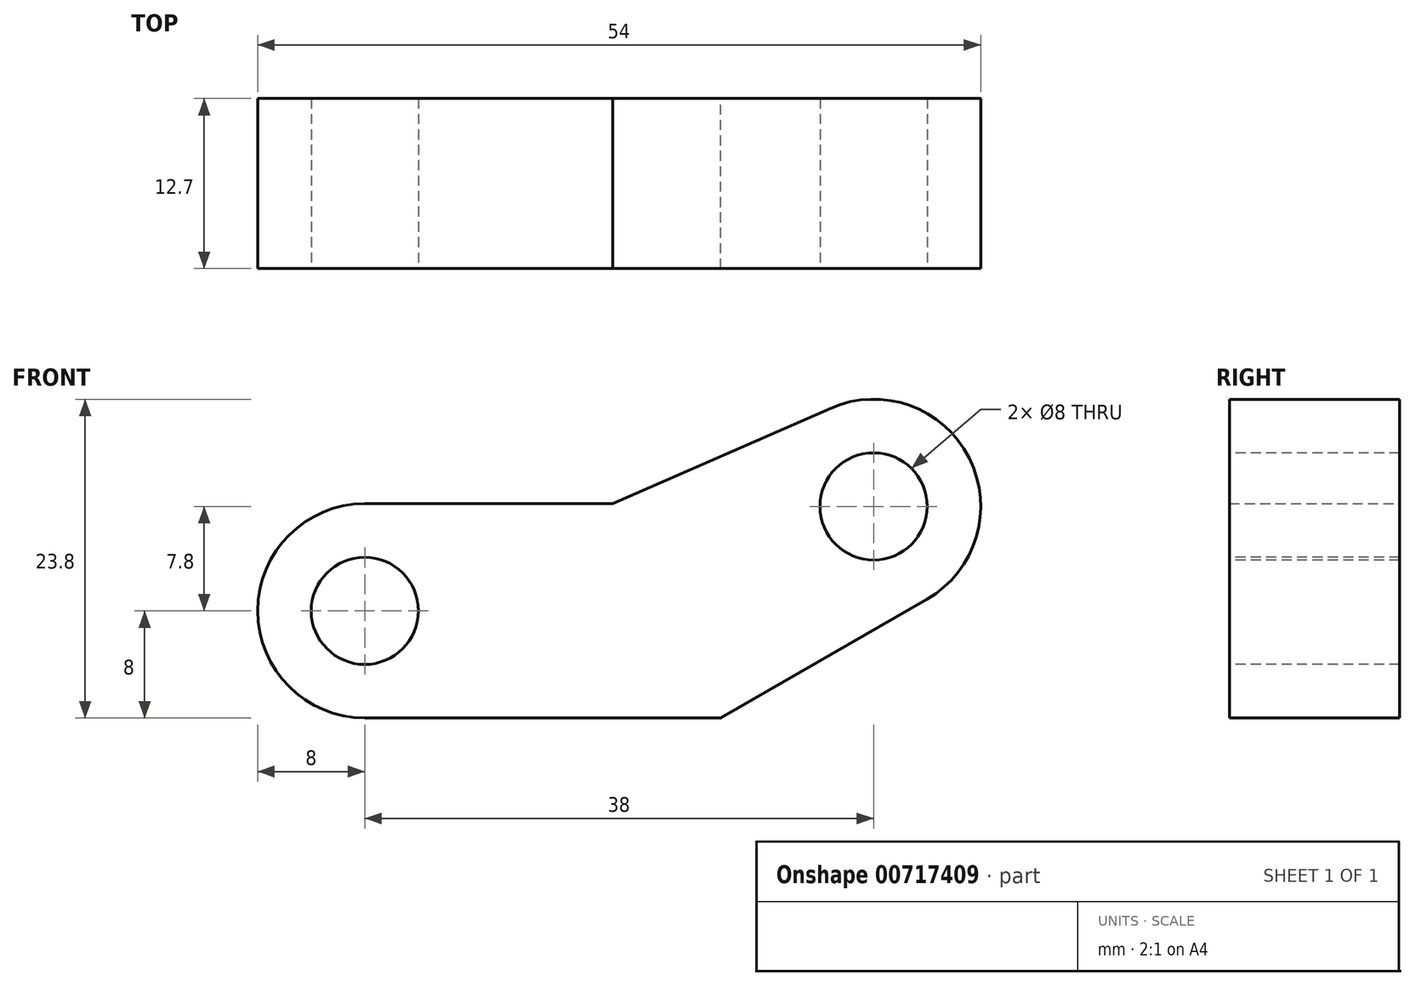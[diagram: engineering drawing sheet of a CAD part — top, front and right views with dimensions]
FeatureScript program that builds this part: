
annotation { "Feature Type Name" : "Feature", "Feature Type Description" : "" }
export const myFeature = defineFeature(function(context is Context, id is Id, definition is map)
    precondition{}
    {
        {
            var Q0;
            Q0=qCreatedBy(makeId("Front.planeOp"),FACE);
            var sketch = newSketch(context, id + "F0", { "sketchPlane" : qUnion([Q0])});
            skLineSegment(sketch, "E0", {"start": v(0, 0) * mm, "end": v(0, 7.8) * mm});
            skLineSegment(sketch, "E1", {"start": v(0, 0) * mm, "end": v(-38, 0) * mm});
            skCircle(sketch, "E2", {"center": v(-38, 0) * mm, "radius": 8 * mm});
            skCircle(sketch, "E3", {"center": v(0, 7.8) * mm, "radius": 8 * mm});
            skLineSegment(sketch, "E4", {"start": v(-38, -8) * mm, "end": v(-11.42, -8) * mm});
            skLineSegment(sketch, "E5", {"start": v(-11.42, -8) * mm, "end": v(3.99, 0.86) * mm});
            skLineSegment(sketch, "E6", {"start": v(-38, 8) * mm, "end": v(-19.5, 8) * mm});
            skLineSegment(sketch, "E7", {"start": v(-19.5, 8) * mm, "end": v(-3.2, 15.13) * mm});
            skSolve(sketch);
        }
        {
            var Q0;
            Q0 = qSketchRegion(id + "F0", true);
            extrude(context, id + "F1", {"entities" : qUnion([Q0]), "depth" : 12.7 * mm, "offsetDistance" : 25.4 * mm});
        }
        {
            var Q0;
            Q0=makeQuery(id+"F1.opExtrude","CAP_FACE",FACE,{"disambiguationData":[OSD([sQuery(id+"F0.wireOp",EDGE,"E2"),sQuery(id+"F0.wireOp",EDGE,"E3"),sQuery(id+"F0.wireOp",EDGE,"E4"),sQuery(id+"F0.wireOp",EDGE,"E5"),sQuery(id+"F0.wireOp",EDGE,"E6"),sQuery(id+"F0.wireOp",EDGE,"E7")])],"isStart":false});
            var sketch = newSketch(context, id + "F2", { "sketchPlane" : qUnion([Q0])});
            skCircle(sketch, "E8", {"center": v(-38, 0) * mm, "radius": 4 * mm});
            skCircle(sketch, "E9", {"center": v(0, 7.8) * mm, "radius": 4 * mm});
            skSolve(sketch);
        }
        {
            var Q0;
            Q0=makeQuery(id+"F2.imprint","IMPRINT",FACE,{"disambiguationData":[TD([[makeQuery(id+"F2.imprint","IMPRINT",EDGE,{"derivedFrom":sQuery(id+"F2.wireOp",EDGE,"E8")}),1.0]])]});
            var Q1;
            Q1=makeQuery(id+"F2.imprint","IMPRINT",FACE,{"disambiguationData":[TD([[makeQuery(id+"F2.imprint","IMPRINT",EDGE,{"derivedFrom":sQuery(id+"F2.wireOp",EDGE,"E9")}),1.0]])]});
            extrude(context, id + "F3", {"entities" : qUnion([Q0, Q1]), "operationType" : NewBodyOperationType.REMOVE, "endBound" : BoundingType.UP_TO_NEXT, "oppositeDirection" : true, "depth" : 25.4 * mm, "offsetDistance" : 25.4 * mm});
        }
    });
